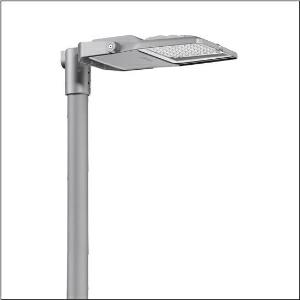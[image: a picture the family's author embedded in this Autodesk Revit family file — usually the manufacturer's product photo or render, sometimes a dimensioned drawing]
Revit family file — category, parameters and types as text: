
# Revit family: floodlight_fl_21_iq_mini___pl33t_5xa7771d4f3a_dbd7
name_source: partatom
category: Lighting Fixtures
units: mm (PartAtom-declared; Revit-internal decimal feet)

## family parameters
Cut with Voids When Loaded = No
Host = Face
Light Source = No
Part Type = Normal
Room Calculation Point = No
Round Connector Dimension = Use Diameter
Shared = No

## types (1)
- --- (1 x LED, 18390 lm, 143 W, 4000K)
    Apparent Load = 143 VA
    CIE Flux Codes = 26 75 99 100 100
    Color Rendering = 70
    Color Temperature = 4000K
    Default Elevation = 1800 mm
    Description = Floodlight FL 21 iQ mini, floodlight, primary light control with lens, of PMMA, primary optical cover: protective disc, of toughened safety glass, transparent, light distribution: PL33T, light emission: direct distribution, installation type: surface-mounted, LED, High Power LED, rated luminous flux: 18.390lm, luminous efficacy: 129lm/W, light colour: 740, colour temperature: 4000K, control: Auto-Match, Temp-Guard, Lumen-Switch, Night-Set, Smart-Wire, Light-Fading, Desk-Remote (wireless, voltage-free reading and setting of iQ features in the workshop via application-optimized NFC function/RFID function), optimised constant luminous flux control (CLO 2.0), with terminal, 6-pole, mains connection: 220..240V, AC, 50/60Hz, start of lifetime: 143W, end of service life: 152W, reduction: 61W, luminaire housing, of diecast aluminium, powder-coated, Siteco® metallic grey (DB 702S), corrosivity category C5 mid according to DIN EN ISO 12944, sealing non-destructively replaceable, please order mast flange separately, mast bracket, of steel, galvanised, powder-coated, Siteco® metallic grey (DB 702S), protection rating (complete): IP66, insulation class (complete): insulation class II (safety insulation), certification: CE, ENEC, VDE, protection symbol: D, impact resistance: IK08, permissible operating ambient temperature: -40..+40°C, permissible operating ambient temperature for outdoor applications: -40..+50°C, standard: DIN EN 12944, LABS conformity tested according to VDMA 24364:2018-05, packaging unit: 1 piece

Light Distribution: PL33T
    Height = 70 mm
    Lamp = 1 x LED
    Lamp Light Flux = 18390 lm
    Lamp Power = 143 W
    Lamp count = 1
    Length = 485 mm
    Luminous efficacy = 129 lm/W
    Manufacturer = Siteco
    ModVariant = No
    Model = 5XA7771D4F3A
    Number of Poles = 1
    OnlyDefault = Yes
    Power Factor = 1
    Product Name = Floodlight FL 21 iQ mini | PL33T
    Product group = floodlight | pylon annexe
    ProductGroupID = 6200
    Protection Class = Protection class II
    Protection Degree = IP 66
    RLX_Detail_Level = 1
    RLX_Emergency_Light_Flux = 0 lm
    RLX_Emergency_Type = 0
    RLX_Emergency_Type_DB = No
    RlxData = <blob elided: 101489 chars, md5=d2c9596f>
    Socket = socket
    Standby Power = 0 W
    System Light Flux = 18390 lm
    System Power = 143 W
    Type Comments = factory setting: luminous flux: 100 % | dim-lin: 254 | 730 mA
    Type Image = l_1007125.jpg
    URL = http://relux.com
    VarID = @adj_081567
    Voltage = 0 V
    Weight = 0.00 kg
    Width = 337 mm

## geometry (parser evidence)
native form markers: Blend x4, Sweep x13
no freeform markers — native parametric forms only
